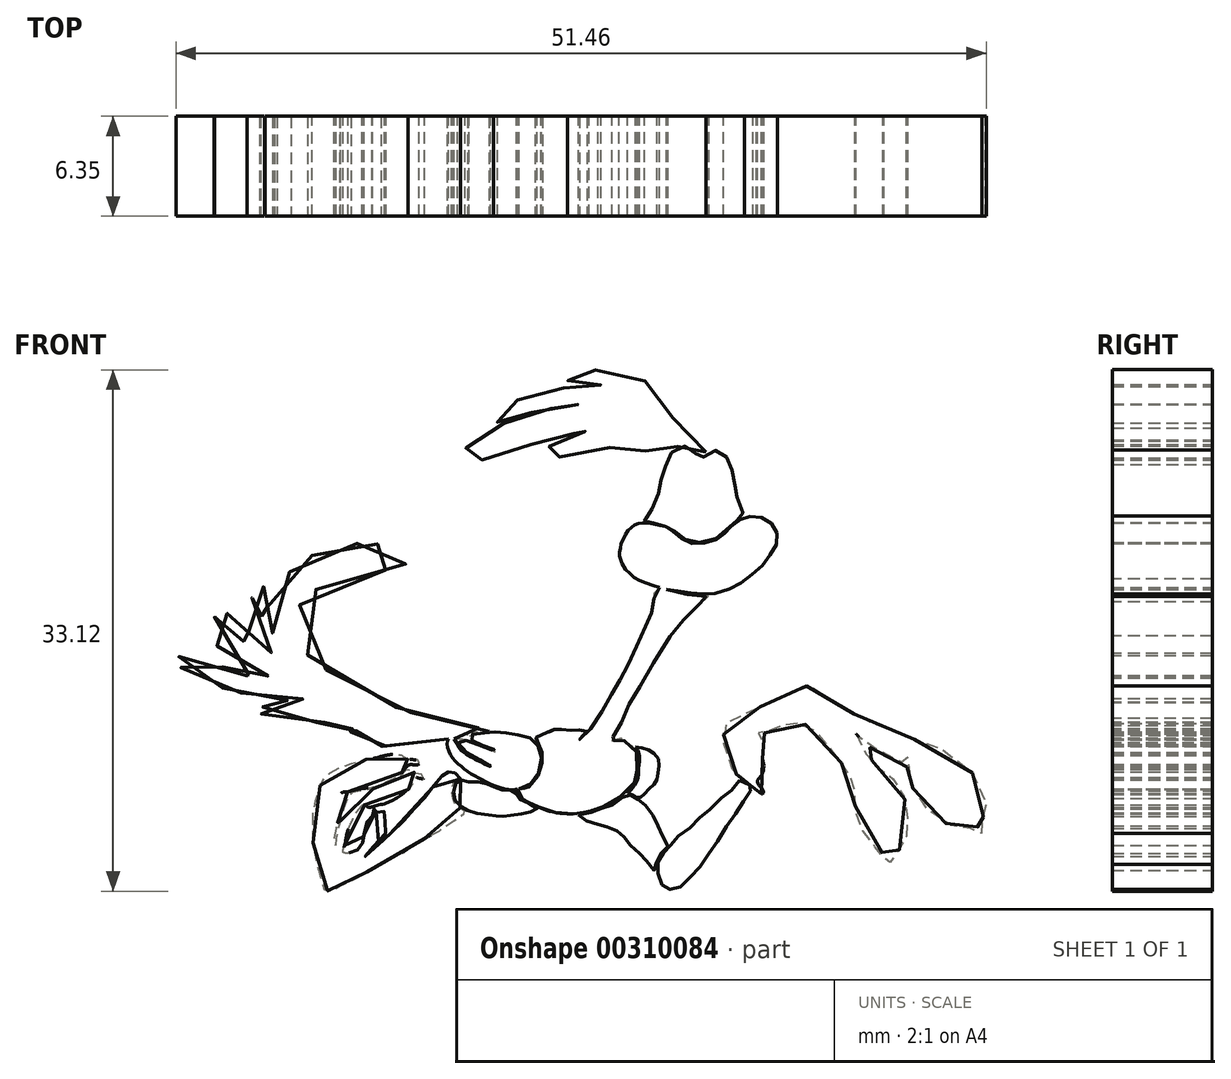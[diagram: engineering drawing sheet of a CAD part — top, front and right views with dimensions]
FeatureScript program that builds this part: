
annotation { "Feature Type Name" : "Feature", "Feature Type Description" : "" }
export const myFeature = defineFeature(function(context is Context, id is Id, definition is map)
    precondition{}
    {
        {
            var Q0;
            Q0=qCreatedBy(makeId("Front.planeOp"),FACE);
            var sketch = newSketch(context, id + "F0", { "sketchPlane" : qUnion([Q0])});
            skFitSpline(sketch, "E0", {"points": [v(9.72, 7.07) * mm, v(9.65, 7.34) * mm, v(9.56, 8.76) * mm, v(9.67, 9.55) * mm, v(9.85, 10.18) * mm, v(10.17, 10.75) * mm, v(10.48, 10.99) * mm, v(10.8, 10.9) * mm, v(11.08, 10.62) * mm, v(11.3, 10.13) * mm, v(11.47, 9.6) * mm, v(11.55, 10.04) * mm, v(11.72, 10.56) * mm, v(11.98, 10.9) * mm, v(12.45, 10.97) * mm, v(12.83, 10.67) * mm, v(13.14, 10.02) * mm, v(13.26, 9.23) * mm, v(13.3, 8.56) * mm, v(13.24, 7.78) * mm, v(12.96, 7.03) * mm, v(12.53, 6.53) * mm, v(12.23, 6.38) * mm, v(12.24, 6.73) * mm, v(12.3, 7.1) * mm, v(12.13, 7.3) * mm, v(11.96, 7.24) * mm, v(11.84, 7.07) * mm, v(11.78, 6.85) * mm, v(11.8, 6.56) * mm, v(11.8, 6.3) * mm, v(11.66, 6.24) * mm, v(11.45, 6.24) * mm, v(11.43, 6.45) * mm, v(11.5, 6.63) * mm, v(11.52, 6.97) * mm, v(11.45, 7.17) * mm, v(11.33, 7.26) * mm, v(11.13, 7.23) * mm, v(10.95, 6.98) * mm, v(10.92, 6.7) * mm, v(10.95, 6.46) * mm, v(10.93, 6.24) * mm, v(10.52, 6.42) * mm, v(10.15, 6.63) * mm, v(9.72, 7.07) * mm]});
            skSolve(sketch);
        }
        {
            var Q0;
            Q0=makeQuery(id+"F0.imprint","IMPRINT",FACE,{"disambiguationData":[TD([[makeQuery(id+"F0.imprint","IMPRINT",EDGE,{"derivedFrom":sQuery(id+"F0.wireOp",EDGE,"E0")}),-1.0]])]});
            extrude(context, id + "F1", {"entities" : qUnion([Q0]), "depth" : 5.08 * mm});
        }
        {
            var Q0;
            Q0=qCreatedBy(makeId("Front.planeOp"),FACE);
            var sketch = newSketch(context, id + "F2", { "sketchPlane" : qUnion([Q0])});
            skFitSpline(sketch, "E1", {"points": [v(7.92, 7.45) * mm, v(8.22, 7.44) * mm, v(8.53, 7.4) * mm, v(8.89, 7.3) * mm, v(9.27, 7.17) * mm, v(9.56, 7.09) * mm, v(9.8, 6.9) * mm, v(10.12, 6.6) * mm, v(10.53, 6.35) * mm, v(10.95, 6.18) * mm, v(11.6, 6.18) * mm, v(12.36, 6.34) * mm, v(12.8, 6.72) * mm, v(13.15, 7) * mm, v(13.47, 7.32) * mm, v(13.89, 7.62) * mm, v(14.28, 7.81) * mm, v(14.05, 8.18) * mm, v(13.8, 8.9) * mm, v(13.71, 9.46) * mm, v(13.7, 9.6) * mm, v(13.6, 10.2) * mm, v(13.47, 10.73) * mm, v(13.38, 11.13) * mm, v(13.06, 11.7) * mm, v(12.7, 12) * mm, v(12.28, 12) * mm, v(11.84, 11.82) * mm, v(11.46, 11.4) * mm, v(11.25, 11.7) * mm, v(10.97, 11.98) * mm, v(10.63, 12.25) * mm, v(10.2, 12.24) * mm, v(9.63, 11.88) * mm, v(9.38, 11.39) * mm, v(9.17, 10.79) * mm, v(9.03, 10.33) * mm, v(8.9, 9.85) * mm, v(8.82, 9.36) * mm, v(8.57, 8.68) * mm, v(8.28, 8.11) * mm, v(8, 7.7) * mm, v(7.92, 7.45) * mm]});
            skSolve(sketch);
        }
        {
            var Q0;
            Q0=qCreatedBy(makeId("Front.planeOp"),FACE);
            var sketch = newSketch(context, id + "F3", { "sketchPlane" : qUnion([Q0])});
            skFitSpline(sketch, "E2", {"points": [v(7.89, 7.39) * mm, v(7.55, 7.38) * mm, v(7.27, 7.25) * mm, v(7.04, 7.06) * mm, v(6.76, 6.78) * mm, v(6.6, 6.43) * mm, v(6.4, 6.03) * mm, v(6.37, 5.63) * mm, v(6.3, 5.5) * mm, v(6.57, 4.65) * mm, v(7.02, 4.15) * mm, v(7.5, 3.8) * mm, v(8.35, 3.47) * mm, v(9.1, 3.22) * mm, v(9.58, 3.14) * mm, v(10.4, 3.02) * mm, v(11.16, 2.9) * mm, v(11.9, 2.88) * mm, v(12.54, 2.95) * mm, v(13.6, 3.34) * mm, v(14.23, 3.73) * mm, v(15, 4.32) * mm, v(15.63, 4.95) * mm, v(16.03, 5.58) * mm, v(16.34, 6.2) * mm, v(16.3, 6.82) * mm, v(15.98, 7.35) * mm, v(15.5, 7.69) * mm, v(14.8, 7.85) * mm, v(14.3, 7.71) * mm, v(13.81, 7.52) * mm, v(13.33, 7.1) * mm, v(13.03, 6.77) * mm, v(12.68, 6.53) * mm, v(12.17, 6.2) * mm, v(11.34, 6.1) * mm, v(10.7, 6.16) * mm, v(10.1, 6.56) * mm, v(9.7, 6.87) * mm, v(9.4, 7.11) * mm, v(8.92, 7.24) * mm, v(8.55, 7.32) * mm, v(8.15, 7.4) * mm, v(7.89, 7.39) * mm]});
            skSolve(sketch);
        }
        {
            var Q0;
            Q0=qCreatedBy(makeId("Front.planeOp"),FACE);
            var sketch = newSketch(context, id + "F4", { "sketchPlane" : qUnion([Q0])});
            skFitSpline(sketch, "E3", {"points": [v(11.83, 11.9) * mm, v(11.38, 12.1) * mm, v(10.85, 12.58) * mm, v(10.25, 13.33) * mm, v(9.7, 14.1) * mm, v(9.06, 14.91) * mm, v(8.86, 15.33) * mm, v(8.4, 15.87) * mm, v(8, 16.35) * mm, v(7.49, 16.78) * mm, v(6.96, 17) * mm, v(6, 17.1) * mm, v(4.65, 17.12) * mm, v(4.13, 17.06) * mm, v(3.8, 16.98) * mm, v(3.35, 16.8) * mm, v(3.16, 16.7) * mm, v(3.08, 16.64) * mm, v(3.01, 16.48) * mm, v(3.34, 16.31) * mm, v(3.7, 16.2) * mm, v(4.2, 16.17) * mm, v(4.52, 16.16) * mm, v(5.04, 16.17) * mm, v(5.14, 16.18) * mm, v(5.13, 16.1) * mm, v(4.32, 16.1) * mm, v(4.03, 16.1) * mm, v(3.78, 16.1) * mm, v(3.28, 16.04) * mm, v(2.52, 15.95) * mm, v(1.51, 15.77) * mm, v(1.35, 15.75) * mm, v(0.62, 15.55) * mm, v(-0.15, 15.21) * mm, v(-0.93, 14.78) * mm, v(-1.35, 14.56) * mm, v(-1.54, 14.38) * mm, v(-1.66, 14.16) * mm, v(-1.59, 13.92) * mm, v(-1.22, 13.76) * mm, v(-0.82, 13.9) * mm, v(-0.66, 13.96) * mm, v(-0.27, 14.13) * mm, v(-0.1, 14.2) * mm, v(0.47, 14.35) * mm, v(1.38, 14.57) * mm, v(1.62, 14.64) * mm, v(2.87, 14.92) * mm, v(3.54, 14.94) * mm, v(3.8, 14.94) * mm, v(4.4, 14.96) * mm, v(4, 14.88) * mm, v(2.84, 14.8) * mm, v(1.55, 14.57) * mm, v(0.7, 14.33) * mm, v(0, 14.14) * mm, v(-0.65, 13.88) * mm, v(-1.35, 13.59) * mm, v(-1.81, 13.4) * mm, v(-2.53, 12.98) * mm, v(-3.18, 12.45) * mm, v(-3.51, 12.05) * mm, v(-3.66, 11.86) * mm, v(-3.78, 11.57) * mm, v(-3.59, 11.16) * mm, v(-2.7, 11.27) * mm, v(-2.44, 11.4) * mm, v(-1.7, 11.6) * mm, v(-0.31, 12.12) * mm, v(-0.12, 12.16) * mm, v(0.69, 12.39) * mm, v(0.85, 12.44) * mm, v(1.58, 12.62) * mm, v(1.73, 12.65) * mm, v(2.53, 12.62) * mm, v(3.49, 13.1) * mm, v(4.04, 13.26) * mm, v(4.48, 13.37) * mm, v(4.97, 13.42) * mm, v(4.92, 13.36) * mm, v(4.36, 13.26) * mm, v(3.66, 13.05) * mm, v(3.01, 12.74) * mm, v(2.5, 12.53) * mm, v(2.36, 12.47) * mm, v(2.06, 12.36) * mm, v(1.58, 12.07) * mm, v(1.34, 11.77) * mm, v(1.39, 11.47) * mm, v(1.53, 11.42) * mm, v(2.04, 11.45) * mm, v(2.23, 11.52) * mm, v(3.86, 11.78) * mm, v(4.25, 11.85) * mm, v(5.07, 11.99) * mm, v(5.28, 12.08) * mm, v(6.35, 12.28) * mm, v(6.55, 12.3) * mm, v(7.23, 12.26) * mm, v(7.44, 12.18) * mm, v(7.57, 12.1) * mm, v(7.73, 12.03) * mm, v(8.49, 11.83) * mm, v(9.15, 11.58) * mm, v(9.37, 11.53) * mm, v(9.53, 11.9) * mm, v(9.84, 12.15) * mm, v(10.13, 12.32) * mm, v(10.57, 12.35) * mm, v(11, 12.07) * mm, v(11.35, 11.6) * mm, v(11.47, 11.54) * mm, v(11.83, 11.9) * mm]});
            skSolve(sketch);
        }
        {
            var Q0;
            Q0=qCreatedBy(makeId("Front.planeOp"),FACE);
            var sketch = newSketch(context, id + "F5", { "sketchPlane" : qUnion([Q0])});
            skFitSpline(sketch, "E4", {"points": [v(8.72, 3.25) * mm, v(9.8, 2.98) * mm, v(10.84, 2.83) * mm, v(11.76, 2.72) * mm, v(12.01, 2.75) * mm, v(11.2, 2.07) * mm, v(10.31, 1.12) * mm, v(9.52, 0.17) * mm, v(8.18, -1.98) * mm, v(7.4, -3.35) * mm, v(6.83, -4.33) * mm, v(6.47, -5.22) * mm, v(6.05, -5.9) * mm, v(5.86, -6.48) * mm, v(5.95, -6.67) * mm, v(6.03, -6.14) * mm, v(6.55, -6.34) * mm, v(7.17, -6.84) * mm, v(7.5, -7.37) * mm, v(7.43, -8.37) * mm, v(7.45, -8.6) * mm, v(7.25, -9.13) * mm, v(6.4, -9.99) * mm, v(5.47, -10.52) * mm, v(5.2, -10.64) * mm, v(4.55, -10.88) * mm, v(3.63, -11.08) * mm, v(3.38, -11.08) * mm, v(2.4, -11.02) * mm, v(1.5, -10.78) * mm, v(0.9, -10.52) * mm, v(0.16, -10.16) * mm, v(-0.22, -9.72) * mm, v(-0.14, -9.5) * mm, v(0.24, -9.52) * mm, v(0.97, -8.96) * mm, v(1.37, -8) * mm, v(1.42, -7.3) * mm, v(1.3, -6.87) * mm, v(1.06, -6.45) * mm, v(0.98, -6.28) * mm, v(1.62, -5.94) * mm, v(1.93, -5.85) * mm, v(2.3, -5.69) * mm, v(2.56, -5.7) * mm, v(3.02, -5.75) * mm, v(3.46, -5.77) * mm, v(3.79, -5.74) * mm, v(4.26, -5.78) * mm, v(3.79, -6.34) * mm, v(4.35, -5.83) * mm, v(5.61, -3.87) * mm, v(6.4, -2.46) * mm, v(7.2, -0.88) * mm, v(8.16, 1.26) * mm, v(8.46, 2.07) * mm, v(8.72, 3.25) * mm]});
            skSolve(sketch);
        }
        {
            var Q0;
            Q0=qCreatedBy(makeId("Front.planeOp"),FACE);
            var sketch = newSketch(context, id + "F6", { "sketchPlane" : qUnion([Q0])});
            skFitSpline(sketch, "E5", {"points": [v(7.35, -6.81) * mm, v(7.84, -6.9) * mm, v(8.28, -7.09) * mm, v(8.72, -7.46) * mm, v(8.85, -7.95) * mm, v(8.76, -8.54) * mm, v(8.67, -8.99) * mm, v(8.4, -9.32) * mm, v(8.03, -9.68) * mm, v(7.74, -9.96) * mm, v(7.5, -10.1) * mm, v(7.27, -9.96) * mm, v(7.02, -9.84) * mm, v(6.85, -9.74) * mm, v(7, -9.6) * mm, v(7.23, -9.33) * mm, v(7.48, -8.92) * mm, v(7.53, -8.57) * mm, v(7.53, -8.18) * mm, v(7.6, -7.61) * mm, v(7.58, -7.33) * mm, v(7.46, -6.98) * mm, v(7.35, -6.81) * mm]});
            skSolve(sketch);
        }
        {
            var Q0;
            Q0=qCreatedBy(makeId("Front.planeOp"),FACE);
            var sketch = newSketch(context, id + "F7", { "sketchPlane" : qUnion([Q0])});
            skFitSpline(sketch, "E6", {"points": [v(3.72, -11.14) * mm, v(4, -11.4) * mm, v(4.69, -11.69) * mm, v(5.25, -11.84) * mm, v(5.65, -11.96) * mm, v(6.17, -12.18) * mm, v(6.5, -12.43) * mm, v(6.81, -12.83) * mm, v(7.2, -13.27) * mm, v(7.75, -13.72) * mm, v(8.07, -14.14) * mm, v(8.54, -14.66) * mm, v(8.64, -14.4) * mm, v(8.74, -13.91) * mm, v(9.04, -13.52) * mm, v(9.4, -13.17) * mm, v(9.14, -12.6) * mm, v(8.84, -11.98) * mm, v(8.62, -11.49) * mm, v(8.2, -10.77) * mm, v(7.78, -10.38) * mm, v(7.4, -10.1) * mm, v(7.13, -9.93) * mm, v(6.81, -9.83) * mm, v(6.34, -10.2) * mm, v(5.7, -10.57) * mm, v(5.1, -10.77) * mm, v(4.54, -10.97) * mm, v(3.72, -11.14) * mm]});
            skSolve(sketch);
        }
        {
            var Q0;
            Q0=qCreatedBy(makeId("Front.planeOp"),FACE);
            var sketch = newSketch(context, id + "F8", { "sketchPlane" : qUnion([Q0])});
            skFitSpline(sketch, "E7", {"points": [v(13.96, -8.94) * mm, v(13.49, -9.51) * mm, v(13.02, -9.88) * mm, v(12.23, -10.65) * mm, v(11.6, -11.14) * mm, v(11, -11.79) * mm, v(10.5, -12.23) * mm, v(9.7, -12.8) * mm, v(9.5, -13.2) * mm, v(9.14, -13.54) * mm, v(8.84, -13.94) * mm, v(8.72, -14.4) * mm, v(8.82, -15.08) * mm, v(9.06, -15.62) * mm, v(9.36, -15.84) * mm, v(9.78, -15.87) * mm, v(10.28, -15.67) * mm, v(10.84, -15.08) * mm, v(11.46, -14.4) * mm, v(12.06, -13.52) * mm, v(12.62, -12.73) * mm, v(13.3, -11.56) * mm, v(13.86, -10.85) * mm, v(14.33, -10.03) * mm, v(14.7, -9.56) * mm, v(14.8, -9.39) * mm, v(14.33, -9.12) * mm, v(13.96, -8.94) * mm]});
            skSolve(sketch);
        }
        {
            var Q0;
            Q0=qCreatedBy(makeId("Front.planeOp"),FACE);
            var sketch = newSketch(context, id + "F9", { "sketchPlane" : qUnion([Q0])});
            skFitSpline(sketch, "E8", {"points": [v(15.36, -9.82) * mm, v(15.2, -9.74) * mm, v(14.99, -9.57) * mm, v(14.9, -9.41) * mm, v(14.8, -9.28) * mm, v(14.42, -9.1) * mm, v(14.12, -8.88) * mm, v(13.87, -8.7) * mm, v(13.6, -8.38) * mm, v(13.32, -8) * mm, v(13.08, -7.44) * mm, v(12.98, -6.76) * mm, v(12.94, -6.4) * mm, v(12.95, -6) * mm, v(12.97, -5.62) * mm, v(13.15, -5.27) * mm, v(13.42, -5.04) * mm, v(14.5, -4.6) * mm, v(15.33, -4.25) * mm, v(16.35, -3.83) * mm, v(17.15, -3.4) * mm, v(17.72, -3.14) * mm, v(17.95, -3) * mm, v(18.3, -2.95) * mm, v(18.8, -3.01) * mm, v(19.26, -3.39) * mm, v(19.95, -3.95) * mm, v(21.06, -4.65) * mm, v(22.38, -5.3) * mm, v(23.42, -5.71) * mm, v(24.33, -6.09) * mm, v(25.46, -6.46) * mm, v(26.84, -7) * mm, v(28.07, -7.77) * mm, v(28.65, -8.35) * mm, v(29.16, -9.2) * mm, v(29.6, -10.12) * mm, v(29.6, -10.66) * mm, v(29.55, -11.01) * mm, v(29.48, -11.19) * mm, v(29.4, -11.31) * mm, v(29.36, -11.44) * mm, v(29.41, -11.6) * mm, v(29.55, -11.85) * mm, v(29.55, -12.1) * mm, v(29.53, -12.3) * mm, v(29.29, -12.3) * mm, v(29.12, -12.12) * mm, v(29.06, -11.9) * mm, v(28.9, -11.86) * mm, v(28.75, -11.98) * mm, v(28.6, -12.02) * mm, v(28.3, -12) * mm, v(27.9, -11.97) * mm, v(27.74, -11.95) * mm, v(27.42, -11.83) * mm, v(26.67, -11.5) * mm, v(26.33, -11.22) * mm, v(25.83, -10.73) * mm, v(25.44, -10.26) * mm, v(25.05, -9.64) * mm, v(24.82, -9.04) * mm, v(24.7, -8.59) * mm, v(24.63, -7.92) * mm, v(24.64, -7.37) * mm, v(24.55, -7.8) * mm, v(24.57, -8.17) * mm, v(24.14, -7.72) * mm, v(23.56, -7.42) * mm, v(23.02, -7.17) * mm, v(22.53, -6.92) * mm, v(22.2, -6.86) * mm, v(21.94, -6.74) * mm, v(21.69, -6.44) * mm, v(21.34, -5.98) * mm, v(21.93, -7.19) * mm, v(22.4, -7.72) * mm, v(22.91, -8.27) * mm, v(23.46, -8.64) * mm, v(23.9, -9.07) * mm, v(24.37, -9.9) * mm, v(24.6, -10.9) * mm, v(24.62, -11.6) * mm, v(24.56, -12.31) * mm, v(24.39, -13.03) * mm, v(24.01, -13.45) * mm, v(23.78, -13.66) * mm, v(23.6, -14.03) * mm, v(23.4, -14.25) * mm, v(23.17, -14.24) * mm, v(23.08, -13.92) * mm, v(23.12, -13.66) * mm, v(22.77, -13.38) * mm, v(22.22, -12.73) * mm, v(21.8, -12.17) * mm, v(21.36, -11.32) * mm, v(21.3, -10.47) * mm, v(21.27, -9.78) * mm, v(21.27, -9.07) * mm, v(21.08, -8.8) * mm, v(20.7, -8.28) * mm, v(20.34, -7.75) * mm, v(19.86, -7.14) * mm, v(19.39, -6.47) * mm, v(18.93, -5.98) * mm, v(18.28, -5.45) * mm, v(17.51, -5.34) * mm, v(16.95, -5.4) * mm, v(16.39, -5.55) * mm, v(15.97, -5.72) * mm, v(15.78, -5.83) * mm, v(15.5, -5.95) * mm, v(15.33, -6) * mm, v(15.2, -5.96) * mm, v(15.02, -5.88) * mm, v(15.28, -6.2) * mm, v(15.43, -6.61) * mm, v(15.35, -7.2) * mm, v(15.49, -7.97) * mm, v(15.32, -8.66) * mm, v(15.1, -8.97) * mm, v(15.27, -9.36) * mm, v(15.4, -9.51) * mm, v(15.48, -9.72) * mm, v(15.36, -9.82) * mm]});
            skSolve(sketch);
        }
        {
            var Q0;
            Q0=qCreatedBy(makeId("Front.planeOp"),FACE);
            var sketch = newSketch(context, id + "F10", { "sketchPlane" : qUnion([Q0])});
            skFitSpline(sketch, "E9", {"points": [v(-3.21, -6.34) * mm, v(-3.17, -6.1) * mm, v(-2.84, -6) * mm, v(-2.37, -5.95) * mm, v(-2, -5.9) * mm, v(-1.74, -5.87) * mm, v(-1.29, -5.9) * mm, v(-1.1, -5.9) * mm, v(-0.38, -6.03) * mm, v(-0.34, -6.03) * mm, v(0.28, -6.1) * mm, v(0.58, -6.2) * mm, v(0.85, -6.38) * mm, v(1.13, -6.72) * mm, v(1.28, -7.26) * mm, v(1.36, -7.62) * mm, v(1.2, -8.36) * mm, v(1.01, -8.8) * mm, v(0.58, -9.25) * mm, v(0.19, -9.42) * mm, v(-0.44, -9.54) * mm, v(-1.03, -9.46) * mm, v(-1.84, -9.19) * mm, v(-2.4, -8.9) * mm, v(-2.93, -8.64) * mm, v(-3.45, -8.3) * mm, v(-3.82, -8) * mm, v(-4.23, -7.6) * mm, v(-4.47, -7.22) * mm, v(-4.62, -6.7) * mm, v(-4.58, -6.42) * mm, v(-4.47, -6.28) * mm, v(-4.11, -6.38) * mm, v(-3.9, -6.83) * mm, v(-3.01, -7.5) * mm, v(-2.32, -7.86) * mm, v(-1.88, -8.05) * mm, v(-2.11, -7.85) * mm, v(-2.71, -7.57) * mm, v(-3.35, -7.2) * mm, v(-3.78, -6.83) * mm, v(-3.96, -6.46) * mm, v(-3.96, -6.4) * mm, v(-3.37, -6.43) * mm, v(-2.9, -6.58) * mm, v(-2.3, -6.83) * mm, v(-1.82, -7.03) * mm, v(-1.42, -7.19) * mm, v(-1.68, -6.96) * mm, v(-2.07, -6.83) * mm, v(-2.55, -6.62) * mm, v(-2.9, -6.46) * mm, v(-3.21, -6.34) * mm]});
            skSolve(sketch);
        }
        {
            var Q0;
            Q0=qCreatedBy(makeId("Front.planeOp"),FACE);
            var sketch = newSketch(context, id + "F11", { "sketchPlane" : qUnion([Q0])});
            skFitSpline(sketch, "E10", {"points": [v(-2.08, -9.18) * mm, v(-2.67, -9.06) * mm, v(-3.24, -9.04) * mm, v(-3.63, -8.93) * mm, v(-3.94, -8.96) * mm, v(-4.1, -9.27) * mm, v(-4.23, -9.85) * mm, v(-4.07, -10.29) * mm, v(-3.67, -10.66) * mm, v(-3.38, -10.83) * mm, v(-2.8, -11.01) * mm, v(-1.92, -11.16) * mm, v(-1.55, -11.2) * mm, v(-1.26, -11.22) * mm, v(-0.9, -11.22) * mm, v(-0.51, -11.16) * mm, v(0.38, -11.03) * mm, v(0.82, -10.91) * mm, v(1.1, -10.74) * mm, v(0.54, -10.42) * mm, v(0, -10.15) * mm, v(-0.24, -9.87) * mm, v(-0.32, -9.6) * mm, v(-0.83, -9.62) * mm, v(-1.26, -9.5) * mm, v(-1.74, -9.33) * mm, v(-2.08, -9.18) * mm]});
            skSolve(sketch);
        }
        {
            var Q0;
            Q0=qCreatedBy(makeId("Front.planeOp"),FACE);
            var sketch = newSketch(context, id + "F12", { "sketchPlane" : qUnion([Q0])});
            skFitSpline(sketch, "E11", {"points": [v(-3.76, -8.86) * mm, v(-3.96, -8.63) * mm, v(-4.12, -8.48) * mm, v(-4.3, -8.43) * mm, v(-4.47, -8.42) * mm, v(-4.58, -8.42) * mm, v(-4.75, -8.53) * mm, v(-4.95, -8.68) * mm, v(-5.3, -9.08) * mm, v(-5.86, -9.8) * mm, v(-6.34, -10.39) * mm, v(-7.01, -11.07) * mm, v(-7.7, -11.83) * mm, v(-8.38, -12.48) * mm, v(-8.67, -12.76) * mm, v(-9.11, -13.12) * mm, v(-9.47, -13.46) * mm, v(-9.85, -13.79) * mm, v(-9.9, -13.72) * mm, v(-8.68, -12.6) * mm, v(-8.55, -12.24) * mm, v(-8.57, -11.62) * mm, v(-8.49, -11.3) * mm, v(-8.7, -10.83) * mm, v(-8.94, -10.8) * mm, v(-9.12, -11) * mm, v(-9.15, -10.7) * mm, v(-9.28, -10.77) * mm, v(-9.4, -10.96) * mm, v(-9.35, -11.2) * mm, v(-9.5, -11.32) * mm, v(-9.7, -11.56) * mm, v(-9.79, -11.9) * mm, v(-9.9, -12.34) * mm, v(-10.01, -12.8) * mm, v(-10, -13.15) * mm, v(-10.3, -13.36) * mm, v(-10.6, -13.49) * mm, v(-10.87, -13.57) * mm, v(-11.12, -13.57) * mm, v(-11.24, -13.48) * mm, v(-11.13, -13.06) * mm, v(-11.04, -12.63) * mm, v(-10.87, -11.97) * mm, v(-10.67, -11.55) * mm, v(-10.47, -11.13) * mm, v(-10.15, -10.69) * mm, v(-9.92, -10.5) * mm, v(-9.59, -10.67) * mm, v(-9.2, -10.57) * mm, v(-8.61, -10.44) * mm, v(-8.06, -10.2) * mm, v(-7.53, -9.88) * mm, v(-7.04, -9.48) * mm, v(-6.76, -9.09) * mm, v(-6.66, -8.76) * mm, v(-6.44, -8.8) * mm, v(-6.07, -8.82) * mm, v(-6.14, -8.65) * mm, v(-6.33, -8.55) * mm, v(-6.6, -8.52) * mm, v(-6.69, -8.46) * mm, v(-6.8, -8.36) * mm, v(-7.1, -8.25) * mm, v(-7.26, -8.31) * mm, v(-7.77, -8.86) * mm, v(-8.28, -9.14) * mm, v(-8.97, -9.39) * mm, v(-9.57, -9.55) * mm, v(-10.23, -9.62) * mm, v(-10.67, -9.72) * mm, v(-10.84, -9.87) * mm, v(-11.19, -10.67) * mm, v(-11.35, -11.38) * mm, v(-11.56, -12.06) * mm, v(-11.68, -12.67) * mm, v(-11.68, -13.08) * mm, v(-11.78, -12.97) * mm, v(-11.73, -12.36) * mm, v(-11.61, -11.83) * mm, v(-11.47, -11.09) * mm, v(-11.17, -10.36) * mm, v(-10.9, -9.8) * mm, v(-11.07, -9.8) * mm, v(-11.38, -9.82) * mm, v(-11.28, -9.72) * mm, v(-10.92, -9.67) * mm, v(-10.26, -9.5) * mm, v(-9.37, -9.39) * mm, v(-8.7, -9.14) * mm, v(-7.82, -8.73) * mm, v(-7.46, -8.41) * mm, v(-7.2, -8.1) * mm, v(-6.96, -7.95) * mm, v(-6.71, -7.97) * mm, v(-6.42, -7.93) * mm, v(-6.42, -7.78) * mm, v(-6.5, -7.67) * mm, v(-6.73, -7.64) * mm, v(-7.1, -7.6) * mm, v(-7.27, -7.52) * mm, v(-7.52, -7.37) * mm, v(-7.8, -7.34) * mm, v(-8.08, -7.3) * mm, v(-8.84, -7.44) * mm, v(-9.12, -7.52) * mm, v(-9.65, -7.6) * mm, v(-10.34, -7.8) * mm, v(-11.15, -8.05) * mm, v(-11.8, -8.33) * mm, v(-12.34, -8.71) * mm, v(-12.62, -9.07) * mm, v(-12.84, -9.73) * mm, v(-13.05, -10.48) * mm, v(-13.2, -11.22) * mm, v(-13.17, -12.03) * mm, v(-13.15, -12.7) * mm, v(-13, -13.68) * mm, v(-12.92, -14.16) * mm, v(-12.77, -14.77) * mm, v(-12.62, -15.3) * mm, v(-12.49, -15.82) * mm, v(-12.13, -15.99) * mm, v(-11.84, -15.92) * mm, v(-11.5, -15.7) * mm, v(-11.1, -15.51) * mm, v(-10.76, -15.36) * mm, v(-10.14, -15.05) * mm, v(-9.86, -14.88) * mm, v(-8.8, -14.26) * mm, v(-7.74, -13.71) * mm, v(-6.9, -13.13) * mm, v(-6.68, -13) * mm, v(-5.97, -12.6) * mm, v(-5.33, -12.27) * mm, v(-4.37, -11.63) * mm, v(-3.77, -11.22) * mm, v(-3.5, -10.95) * mm, v(-3.7, -10.75) * mm, v(-4.07, -10.5) * mm, v(-4.2, -10.24) * mm, v(-4.3, -9.8) * mm, v(-4.32, -9.47) * mm, v(-4.22, -9.2) * mm, v(-4.14, -8.97) * mm, v(-4.04, -8.86) * mm, v(-3.76, -8.86) * mm]});
            skSolve(sketch);
        }
        {
            var Q0;
            Q0=qCreatedBy(makeId("Front.planeOp"),FACE);
            var sketch = newSketch(context, id + "F13", { "sketchPlane" : qUnion([Q0])});
            skFitSpline(sketch, "E12", {"points": [v(-1.95, -5.82) * mm, v(-3.41, -5.5) * mm, v(-4.28, -5.4) * mm, v(-4.93, -5.14) * mm, v(-6.6, -4.7) * mm, v(-7.15, -4.58) * mm, v(-8.5, -4.01) * mm, v(-10.36, -3.1) * mm, v(-11.49, -2.47) * mm, v(-12.8, -1.55) * mm, v(-13.94, -0.6) * mm, v(-14.44, 0) * mm, v(-14.5, 0.92) * mm, v(-14.14, 1.93) * mm, v(-13.47, 2.82) * mm, v(-12.4, 3.47) * mm, v(-10.82, 4.03) * mm, v(-8.82, 4.36) * mm, v(-7.9, 4.53) * mm, v(-7.23, 4.8) * mm, v(-7.16, 5.35) * mm, v(-7.62, 5.72) * mm, v(-8.23, 5.96) * mm, v(-9, 6.07) * mm, v(-9.29, 6.07) * mm, v(-10.16, 6.12) * mm, v(-10.47, 6.09) * mm, v(-11.14, 6.03) * mm, v(-12.21, 5.71) * mm, v(-13.2, 5.34) * mm, v(-13.97, 4.9) * mm, v(-14.58, 4.32) * mm, v(-15.2, 3.71) * mm, v(-15.71, 2.93) * mm, v(-15.96, 2.27) * mm, v(-16.2, 1.4) * mm, v(-16.01, 0.75) * mm, v(-15.66, 0.38) * mm, v(-15.57, 0.34) * mm, v(-15.77, 0.23) * mm, v(-16.16, 0.8) * mm, v(-16.36, 1.27) * mm, v(-16.46, 1.93) * mm, v(-16.4, 2.66) * mm, v(-16.3, 3.27) * mm, v(-16.23, 3.75) * mm, v(-16.27, 3.86) * mm, v(-16.79, 3.29) * mm, v(-17.03, 2.6) * mm, v(-17.14, 1.91) * mm, v(-17.3, 1.23) * mm, v(-17.2, 0.23) * mm, v(-17.05, -0.14) * mm, v(-16.33, -0.66) * mm, v(-15.71, -0.86) * mm, v(-16.38, -0.8) * mm, v(-16.96, -0.42) * mm, v(-17.73, 0) * mm, v(-18.27, 0.9) * mm, v(-18.55, 1.53) * mm, v(-18.73, 2.2) * mm, v(-18.92, 2.4) * mm, v(-19.16, 2.25) * mm, v(-19.38, 1.78) * mm, v(-19.38, 0.77) * mm, v(-19.4, 0) * mm, v(-19.09, -0.66) * mm, v(-18.51, -1.5) * mm, v(-17.8, -1.9) * mm, v(-17.27, -2.16) * mm, v(-17, -2.22) * mm, v(-16.62, -2.33) * mm, v(-15.79, -2.33) * mm, v(-15.42, -2.38) * mm, v(-15.75, -2.4) * mm, v(-16.64, -2.46) * mm, v(-17.29, -2.3) * mm, v(-18.29, -2) * mm, v(-19.12, -1.62) * mm, v(-20.12, -1.33) * mm, v(-20.96, -1.16) * mm, v(-21.4, -1.05) * mm, v(-21.7, -1.09) * mm, v(-21.8, -1.1) * mm, v(-21.8, -1.46) * mm, v(-21.2, -2.01) * mm, v(-20.4, -2.44) * mm, v(-19.73, -2.83) * mm, v(-19.18, -3) * mm, v(-18.86, -3.07) * mm, v(-18.03, -3.31) * mm, v(-17.14, -3.55) * mm, v(-16.25, -3.87) * mm, v(-15.88, -4.03) * mm, v(-15.5, -3.96) * mm, v(-14.84, -3.86) * mm, v(-14.08, -3.83) * mm, v(-13.5, -3.8) * mm, v(-13.53, -3.94) * mm, v(-14.29, -4) * mm, v(-15.12, -4.05) * mm, v(-16.05, -4.2) * mm, v(-16.53, -4.44) * mm, v(-16.42, -4.74) * mm, v(-15.53, -4.96) * mm, v(-15.16, -5.1) * mm, v(-14.25, -5.16) * mm, v(-13.23, -5.27) * mm, v(-12.92, -5.27) * mm, v(-12.43, -5.27) * mm, v(-11.7, -5.3) * mm, v(-10.93, -5.1) * mm, v(-10.71, -5.01) * mm, v(-11.2, -5.3) * mm, v(-11.45, -5.42) * mm, v(-11.16, -5.64) * mm, v(-10.7, -5.68) * mm, v(-10.16, -5.6) * mm, v(-9.38, -5.55) * mm, v(-8.84, -5.51) * mm, v(-8.88, -5.6) * mm, v(-9.77, -5.75) * mm, v(-10.08, -5.79) * mm, v(-10.91, -5.9) * mm, v(-11.41, -6.14) * mm, v(-11.34, -6.42) * mm, v(-10.67, -6.64) * mm, v(-10.3, -6.66) * mm, v(-9.8, -6.68) * mm, v(-8.82, -6.79) * mm, v(-7.49, -6.59) * mm, v(-6.28, -6.59) * mm, v(-5.95, -6.6) * mm, v(-5, -6.57) * mm, v(-4.7, -6.55) * mm, v(-4.67, -6.34) * mm, v(-4.39, -6.33) * mm, v(-4.09, -6.31) * mm, v(-3.8, -6.29) * mm, v(-3.32, -6.36) * mm, v(-3.32, -6.2) * mm, v(-3.23, -5.92) * mm, v(-2.84, -5.88) * mm, v(-2.28, -5.88) * mm, v(-1.95, -5.82) * mm]});
            skSolve(sketch);
        }
        {
            var Q0;
            Q0=makeQuery(id+"F9.imprint","IMPRINT",FACE,{"disambiguationData":[TD([[makeQuery(id+"F9.imprint","IMPRINT",EDGE,{"derivedFrom":sQuery(id+"F9.wireOp",EDGE,"E8")}),-1.0]])]});
            var Q1;
            Q1=makeQuery(id+"F8.imprint","IMPRINT",FACE,{"disambiguationData":[TD([[makeQuery(id+"F8.imprint","IMPRINT",EDGE,{"derivedFrom":sQuery(id+"F8.wireOp",EDGE,"E7")}),1.0]])]});
            var Q2;
            Q2=makeQuery(id+"F7.imprint","IMPRINT",FACE,{"disambiguationData":[TD([[makeQuery(id+"F7.imprint","IMPRINT",EDGE,{"derivedFrom":sQuery(id+"F7.wireOp",EDGE,"E6")}),1.0]])]});
            var Q3;
            Q3=makeQuery(id+"F6.imprint","IMPRINT",FACE,{"disambiguationData":[TD([[makeQuery(id+"F6.imprint","IMPRINT",EDGE,{"derivedFrom":sQuery(id+"F6.wireOp",EDGE,"E5")}),-1.0]])]});
            var Q4;
            Q4=makeQuery(id+"F5.imprint","IMPRINT",FACE,{"disambiguationData":[TD([[makeQuery(id+"F5.imprint","IMPRINT",EDGE,{"derivedFrom":sQuery(id+"F5.wireOp",EDGE,"E4")}),-1.0]])]});
            var Q5;
            Q5=makeQuery(id+"F10.imprint","IMPRINT",FACE,{"disambiguationData":[TD([[makeQuery(id+"F10.imprint","IMPRINT",EDGE,{"derivedFrom":sQuery(id+"F10.wireOp",EDGE,"E9")}),-1.0]])]});
            var Q6;
            Q6=makeQuery(id+"F11.imprint","IMPRINT",FACE,{"disambiguationData":[TD([[makeQuery(id+"F11.imprint","IMPRINT",EDGE,{"derivedFrom":sQuery(id+"F11.wireOp",EDGE,"E10")}),1.0]])]});
            var Q7;
            Q7=makeQuery(id+"F12.imprint","IMPRINT",FACE,{"disambiguationData":[TD([[makeQuery(id+"F12.imprint","IMPRINT",EDGE,{"derivedFrom":sQuery(id+"F12.wireOp",EDGE,"E11")}),1.0]])]});
            var Q8;
            Q8=makeQuery(id+"F13.imprint","IMPRINT",FACE,{"disambiguationData":[TD([[makeQuery(id+"F13.imprint","IMPRINT",EDGE,{"derivedFrom":sQuery(id+"F13.wireOp",EDGE,"E12")}),1.0]])]});
            var Q9;
            Q9=makeQuery(id+"F3.imprint","IMPRINT",FACE,{"disambiguationData":[TD([[makeQuery(id+"F3.imprint","IMPRINT",EDGE,{"derivedFrom":sQuery(id+"F3.wireOp",EDGE,"E2")}),1.0]])]});
            var Q10;
            Q10=makeQuery(id+"F4.imprint","IMPRINT",FACE,{"disambiguationData":[TD([[makeQuery(id+"F4.imprint","IMPRINT",EDGE,{"derivedFrom":sQuery(id+"F4.wireOp",EDGE,"E3")}),1.0]])]});
            var Q11;
            Q11=makeQuery(id+"F2.imprint","IMPRINT",FACE,{"disambiguationData":[TD([[makeQuery(id+"F2.imprint","IMPRINT",EDGE,{"derivedFrom":sQuery(id+"F2.wireOp",EDGE,"E1")}),1.0]])]});
            extrude(context, id + "F14", {"entities" : qUnion([Q0, Q1, Q2, Q3, Q4, Q5, Q6, Q7, Q8, Q9, Q10, Q11]), "operationType" : NewBodyOperationType.ADD, "depth" : 6.35 * mm});
        }
    });
